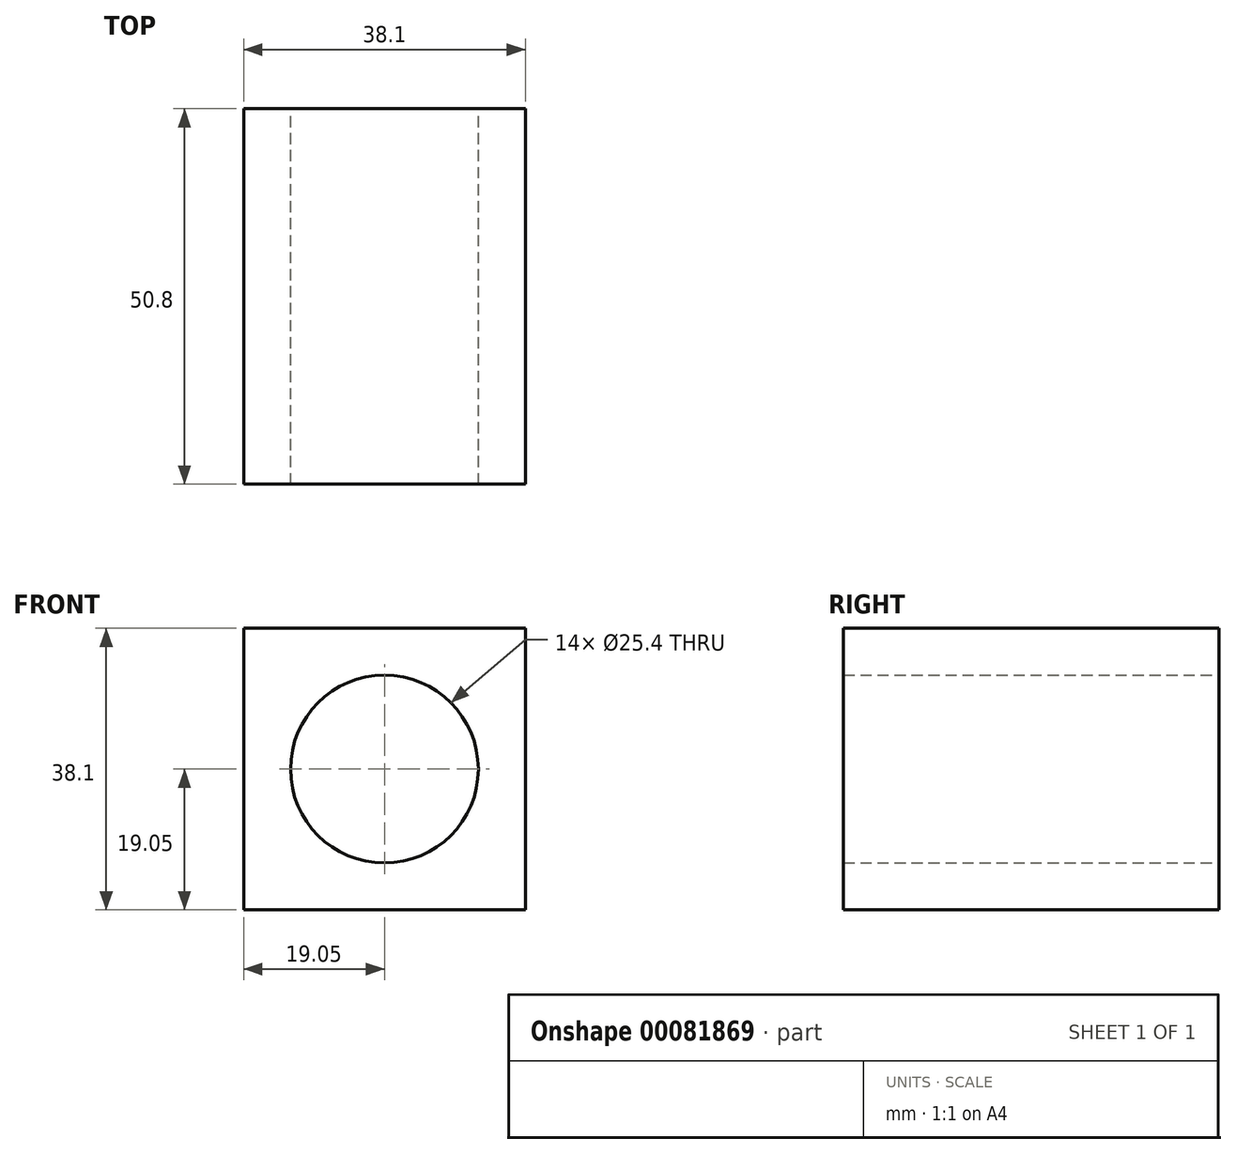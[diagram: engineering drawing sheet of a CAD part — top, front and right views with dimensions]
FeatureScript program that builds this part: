
annotation { "Feature Type Name" : "Feature", "Feature Type Description" : "" }
export const myFeature = defineFeature(function(context is Context, id is Id, definition is map)
    precondition{}
    {
        {
            var Q0;
            Q0=qCreatedBy(makeId("Front.planeOp"),FACE);
            var sketch = newSketch(context, id + "F0", { "sketchPlane" : qUnion([Q0])});
            skCircle(sketch, "E0", {"center": v(0, 0) * mm, "radius": 12.7 * mm});
            skLineSegment(sketch, "E1.bottom", {"start": v(19.05, 19.05) * mm, "end": v(-19.05, 19.05) * mm});
            skLineSegment(sketch, "E1.top", {"start": v(19.05, -19.05) * mm, "end": v(-19.05, -19.05) * mm});
            skLineSegment(sketch, "E1.left", {"start": v(19.05, 19.05) * mm, "end": v(19.05, -19.05) * mm});
            skLineSegment(sketch, "E1.right", {"start": v(-19.05, 19.05) * mm, "end": v(-19.05, -19.05) * mm});
            skSolve(sketch);
        }
        {
            var Q0;
            Q0=makeQuery(id+"F0.imprint","IMPRINT",FACE,{"disambiguationData":[TD([[makeQuery(id+"F0.imprint","IMPRINT",EDGE,{"derivedFrom":sQuery(id+"F0.wireOp",EDGE,"E0")}),-1.0]])]});
            extrude(context, id + "F1", {"entities" : qUnion([Q0]), "depth" : 50.8 * mm});
        }
    });
